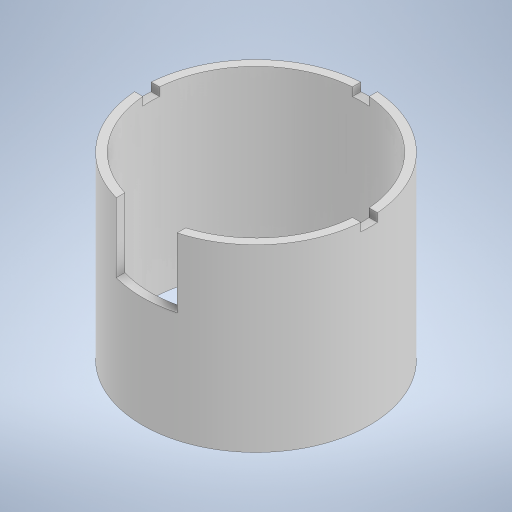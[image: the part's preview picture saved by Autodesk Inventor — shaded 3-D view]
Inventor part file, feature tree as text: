
AUTODESK INVENTOR PART (.ipt)
format: ipt  version: 2024 (Build 280153000, 153)  size: 241,152 bytes
history: native  units: in
note: dims shown in document units (in); Inventor stores cm internally (conversion verified against a paired STEP export)
features: extrude x5, sketch x5
ambient origin geometry x8: Origin, YZ Plane, XZ Plane, XY Plane, X Axis, Y Axis, Z Axis, Center Point
bodies: Solid1 (feature_tree)
feature tree (10):
  extrude  "Extrusion1"  Depth=2.9921in
  extrude  "Extrusion2"  Depth=2.5591in
  extrude  "Extrusion3"  Depth=0.1181in TaperAngle=0.0deg
  extrude  "Extrusion4"  Depth=0.1181in
  extrude  "Extrusion5"  Depth=0.1181in TaperAngle=0.0deg
  sketch  "Sketch1"  dims[d0=3.2283in d1=2.9921in]
  sketch  "Sketch2"  dims[d2=2.5591in d3=0.0in d4=0.2362in]
  sketch  "Sketch3"  dims[d5=3.2283in d6=0.1181in d7=0.0in]
  sketch  "Sketch4"  dims[d8=0.1181in d9=0.2362in]
  sketch  "Sketch5"  dims[d10=3.2283in d11=0.1181in d12=0.0in d13=0.2362in d14=3.2283in d15=0.0in d16=0.4331in d17=0.0in d18=0.8661in d19=3.2283in d20=0.9843in d21=0.0in]
